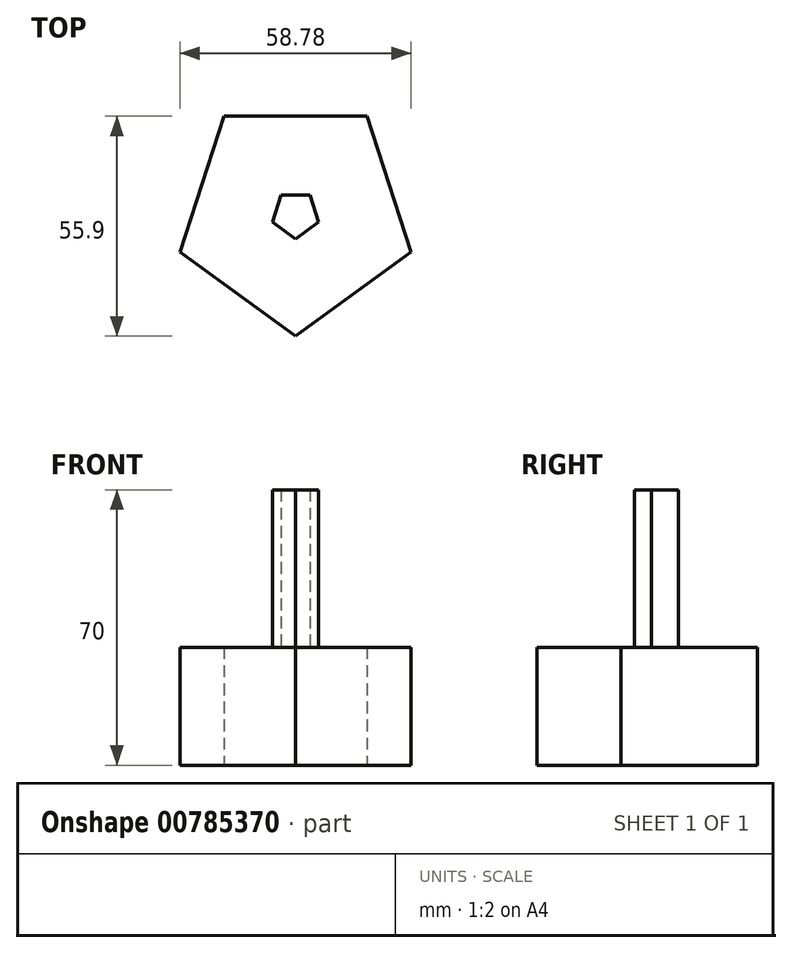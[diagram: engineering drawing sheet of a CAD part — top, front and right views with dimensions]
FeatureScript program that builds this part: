
annotation { "Feature Type Name" : "Feature", "Feature Type Description" : "" }
export const myFeature = defineFeature(function(context is Context, id is Id, definition is map)
    precondition{}
    {
        {
            var Q0;
            Q0=qCreatedBy(makeId("Top.planeOp"),FACE);
            var sketch = newSketch(context, id + "F0", { "sketchPlane" : qUnion([Q0])});
            skCircle(sketch, "E0.cCircle", {"center": v(0, 0) * mm, "radius": 25 * mm, "construction": true});
            skLineSegment(sketch, "E0.0", {"start": v(-18.16, 25) * mm, "end": v(18.16, 25) * mm});
            skLineSegment(sketch, "E0.1", {"start": v(18.16, 25) * mm, "end": v(29.39, -9.55) * mm});
            skLineSegment(sketch, "E0.2", {"start": v(29.39, -9.55) * mm, "end": v(0, -30.9) * mm});
            skLineSegment(sketch, "E0.3", {"start": v(0, -30.9) * mm, "end": v(-29.39, -9.55) * mm});
            skLineSegment(sketch, "E0.4", {"start": v(-29.39, -9.55) * mm, "end": v(-18.16, 25) * mm});
            skPoint(sketch, "E0.0.midPoint", {"position": v(0, 25) * mm});
            skSolve(sketch);
        }
        {
            var Q0;
            Q0=makeQuery(id+"F0.imprint","IMPRINT",FACE,{"disambiguationData":[TD([[makeQuery(id+"F0.imprint","IMPRINT",EDGE,{"derivedFrom":sQuery(id+"F0.wireOp",EDGE,"E0.0")}),-1.0]])]});
            extrude(context, id + "F1", {"entities" : qUnion([Q0]), "depth" : 30 * mm, "offsetDistance" : 25 * mm});
        }
        {
            var Q0;
            Q0=makeQuery(id+"F1.opExtrude","CAP_FACE",FACE,{"disambiguationData":[OSD([sQuery(id+"F0.wireOp",EDGE,"E0.0"),sQuery(id+"F0.wireOp",EDGE,"E0.1"),sQuery(id+"F0.wireOp",EDGE,"E0.2"),sQuery(id+"F0.wireOp",EDGE,"E0.3"),sQuery(id+"F0.wireOp",EDGE,"E0.4")])],"isStart":false});
            var sketch = newSketch(context, id + "F2", { "sketchPlane" : qUnion([Q0])});
            skPoint(sketch, "E1.cCircle.perimeterSnap0", {"position": v(-23.78, 7.73) * mm});
            skPoint(sketch, "E1.0.midPoint.positionSnap0", {"position": v(-23.78, 7.73) * mm});
            skCircle(sketch, "E2.cCircle", {"center": v(0, 0) * mm, "radius": 5 * mm, "construction": true});
            skLineSegment(sketch, "E2.0", {"start": v(0, -6.18) * mm, "end": v(-5.88, -1.9) * mm});
            skLineSegment(sketch, "E2.1", {"start": v(-5.88, -1.9) * mm, "end": v(-3.63, 5) * mm});
            skLineSegment(sketch, "E2.2", {"start": v(-3.63, 5) * mm, "end": v(3.63, 5) * mm});
            skLineSegment(sketch, "E2.3", {"start": v(3.63, 5) * mm, "end": v(5.88, -1.9) * mm});
            skLineSegment(sketch, "E2.4", {"start": v(5.88, -1.9) * mm, "end": v(0, -6.18) * mm});
            skPoint(sketch, "E2.0.midPoint", {"position": v(-2.94, -4.05) * mm});
            skSolve(sketch);
        }
        {
            var Q0;
            Q0=makeQuery(id+"F2.imprint","IMPRINT",FACE,{"disambiguationData":[TD([[makeQuery(id+"F2.imprint","IMPRINT",EDGE,{"derivedFrom":sQuery(id+"F2.wireOp",EDGE,"E2.0")}),-1.0]])]});
            extrude(context, id + "F3", {"entities" : qUnion([Q0]), "operationType" : NewBodyOperationType.ADD, "depth" : 40 * mm, "offsetDistance" : 25 * mm});
        }
    });
